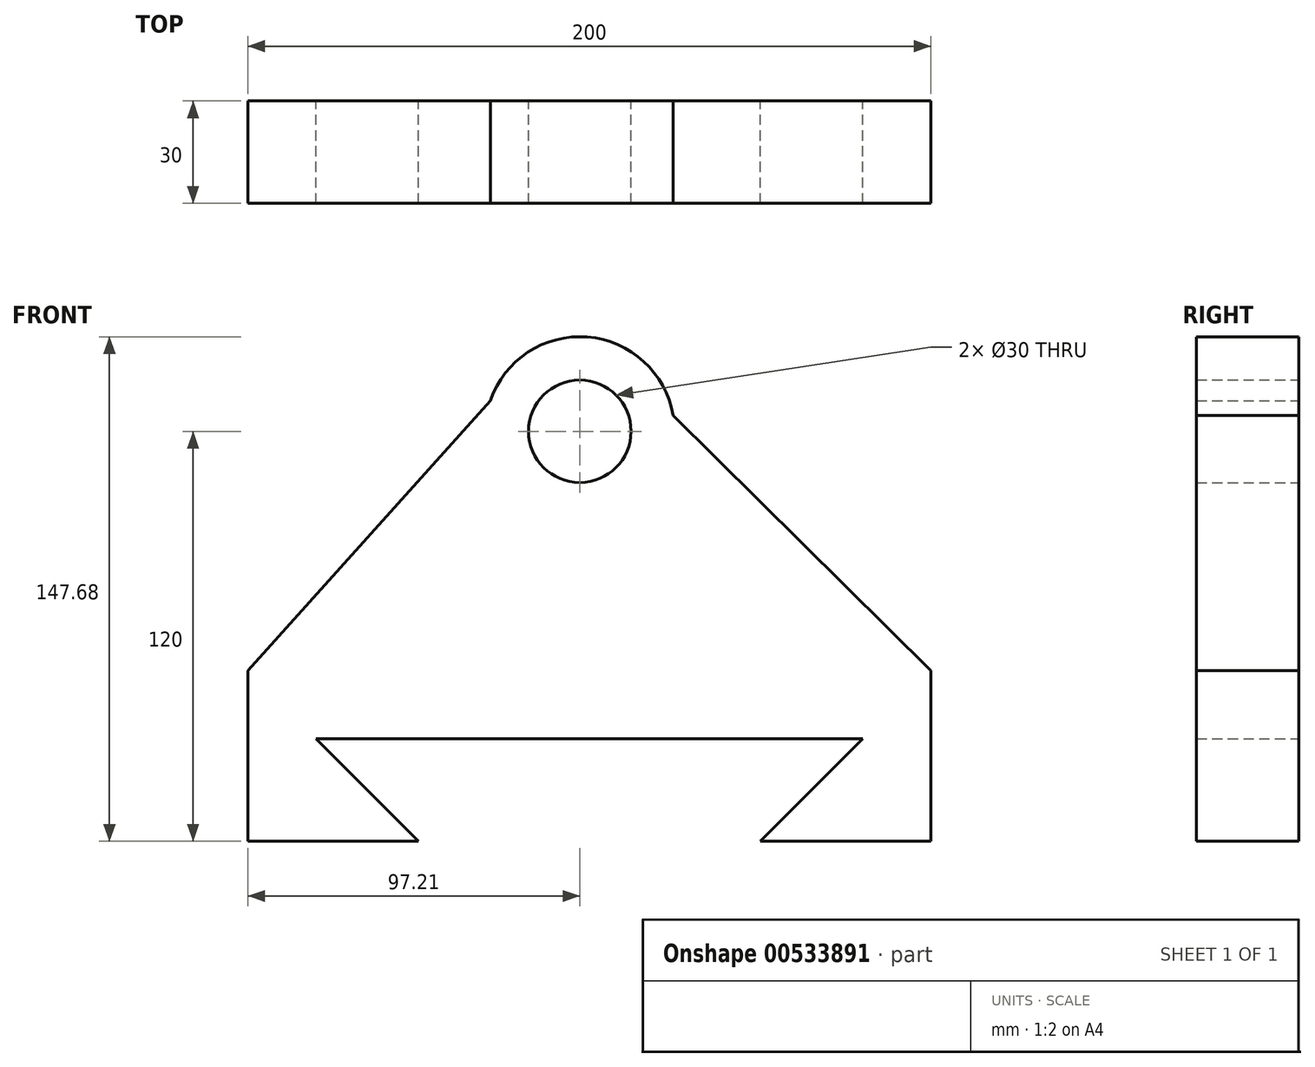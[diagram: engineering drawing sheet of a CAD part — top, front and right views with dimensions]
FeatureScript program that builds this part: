
annotation { "Feature Type Name" : "Feature", "Feature Type Description" : "" }
export const myFeature = defineFeature(function(context is Context, id is Id, definition is map)
    precondition{}
    {
        {
            var Q0;
            Q0=qCreatedBy(makeId("Front.planeOp"),FACE);
            var sketch = newSketch(context, id + "F0", { "sketchPlane" : qUnion([Q0])});
            skLineSegment(sketch, "E0", {"start": v(-97.2, 0) * mm, "end": v(102.8, 0) * mm});
            skLineSegment(sketch, "E1", {"start": v(102.8, 0) * mm, "end": v(102.8, -50) * mm});
            skLineSegment(sketch, "E2", {"start": v(102.8, -50) * mm, "end": v(52.8, -50) * mm});
            skLineSegment(sketch, "E3", {"start": v(52.8, -50) * mm, "end": v(82.8, -20) * mm});
            skLineSegment(sketch, "E4", {"start": v(82.8, -20) * mm, "end": v(-77.2, -20) * mm});
            skLineSegment(sketch, "E5", {"start": v(-77.2, -20) * mm, "end": v(-47.2, -50) * mm});
            skLineSegment(sketch, "E6", {"start": v(-47.2, -50) * mm, "end": v(-97.2, -50) * mm});
            skLineSegment(sketch, "E7", {"start": v(-97.2, 0) * mm, "end": v(-97.2, -50) * mm});
            skCircle(sketch, "E8", {"center": v(0, 70) * mm, "radius": 15 * mm});
            skCircle(sketch, "E9", {"center": v(0, 70) * mm, "radius": 27.68 * mm});
            skLineSegment(sketch, "E10", {"start": v(-97.2, 0) * mm, "end": v(-26.2, 78.95) * mm});
            skLineSegment(sketch, "E11", {"start": v(102.8, 0) * mm, "end": v(27.28, 74.67) * mm});
            skSolve(sketch);
        }
        {
            var Q0;
            Q0 = qSketchRegion(id + "F0", true);
            extrude(context, id + "F1", {"entities" : qUnion([Q0]), "depth" : 30 * mm, "offsetDistance" : 25 * mm});
        }
    });
